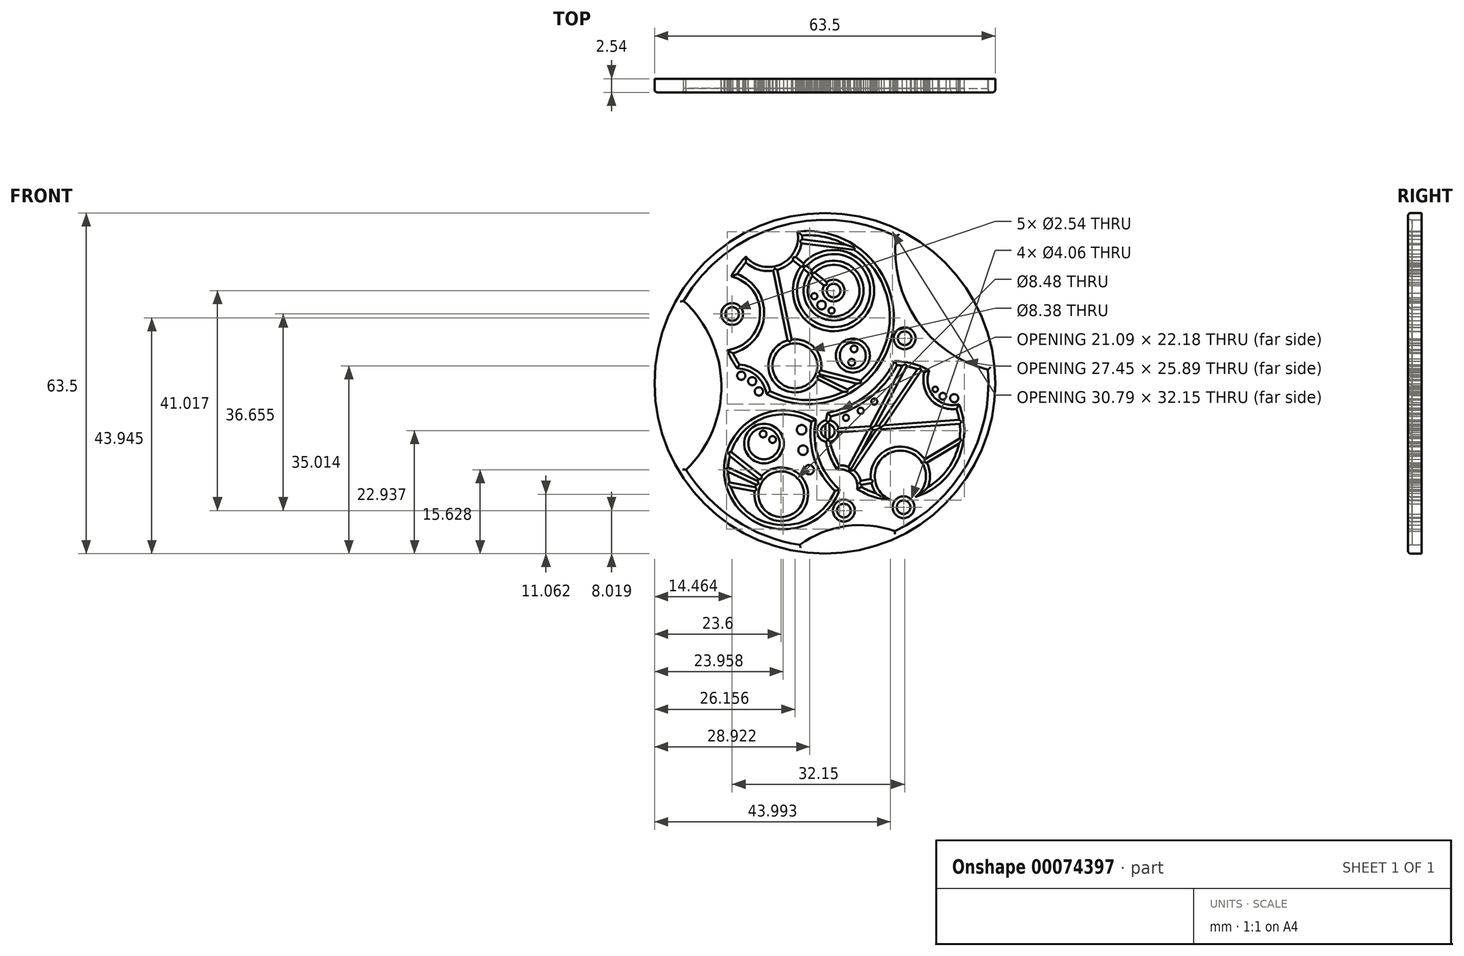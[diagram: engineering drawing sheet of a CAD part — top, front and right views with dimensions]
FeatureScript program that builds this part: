
annotation { "Feature Type Name" : "Feature", "Feature Type Description" : "" }
export const myFeature = defineFeature(function(context is Context, id is Id, definition is map)
    precondition{}
    {
        {
            var Q0;
            Q0=qCreatedBy(makeId("Front.planeOp"),FACE);
            var sketch = newSketch(context, id + "F0", { "sketchPlane" : qUnion([Q0])});
            skCircle(sketch, "E0", {"center": v(0, 0) * mm, "radius": 31.75 * mm});
            skCircle(sketch, "E1", {"center": v(-8.15, -20.69) * mm, "radius": 5 * mm});
            skCircle(sketch, "E2", {"center": v(-11.36, -11.23) * mm, "radius": 3.69 * mm});
            skArc(sketch, "E3", {"start": v(13.02, -27.56) * mm, "mid": v(26.4, -15.22) * mm, "end": v(30.37, 2.55) * mm});
            skArc(sketch, "E4", {"start": v(-18.22, 6.19) * mm, "mid": v(-17.38, 4.42) * mm, "end": v(-16.33, 2.77) * mm});
            skArc(sketch, "E5", {"start": v(16.87, -21.2) * mm, "mid": v(24.74, -14.34) * mm, "end": v(25, -3.9) * mm});
            skPoint(sketch, "E6", {"position": v(31.75, -0.45) * mm});
            skPoint(sketch, "E7", {"position": v(31.42, -4.58) * mm});
            skPoint(sketch, "E8", {"position": v(30.4, -2.2) * mm});
            skCircle(sketch, "E9", {"center": v(3.54, -23.73) * mm, "radius": 1.27 * mm});
            skCircle(sketch, "E10", {"center": v(14.67, -23.1) * mm, "radius": 1.27 * mm});
            skCircle(sketch, "E11", {"center": v(-5.6, 3.26) * mm, "radius": 4.95 * mm});
            skCircle(sketch, "E12", {"center": v(5.2, 5.17) * mm, "radius": 3.18 * mm});
            skCircle(sketch, "E13", {"center": v(1.62, 17.29) * mm, "radius": 1.27 * mm});
            skCircle(sketch, "E14", {"center": v(1.62, 17.29) * mm, "radius": 5.58 * mm});
            skCircle(sketch, "E15", {"center": v(1.62, 17.29) * mm, "radius": 6.81 * mm});
            skCircle(sketch, "E16", {"center": v(14.86, 8.39) * mm, "radius": 1.27 * mm});
            skCircle(sketch, "E17", {"center": v(-17.29, 12.92) * mm, "radius": 1.27 * mm});
            skArc(sketch, "E18", {"start": v(16.87, -21.2) * mm, "mid": v(13.48, -12.59) * mm, "end": v(12.28, -21.76) * mm});
            skArc(sketch, "E19", {"start": v(6.02, -19.73) * mm, "mid": v(5.1, -16.94) * mm, "end": v(2.3, -16.1) * mm});
            skArc(sketch, "E20.trimOffspring", {"start": v(6.02, -19.73) * mm, "mid": v(9.02, -21.15) * mm, "end": v(12.28, -21.76) * mm});
            skArc(sketch, "E21", {"start": v(-1.7, -6.78) * mm, "mid": v(-1.2, -13.9) * mm, "end": v(2.75, -19.84) * mm});
            skPoint(sketch, "E22.center.orphan", {"position": v(-7.7, -16.12) * mm});
            skArc(sketch, "E23", {"start": v(19.46, 2.42) * mm, "mid": v(20.27, -2.46) * mm, "end": v(25, -3.9) * mm});
            skArc(sketch, "E24.trimOffspring", {"start": v(19.46, 2.42) * mm, "mid": v(16.34, 3.7) * mm, "end": v(13, 4.13) * mm});
            skArc(sketch, "E25", {"start": v(0.49, -5.54) * mm, "mid": v(7.84, -2.14) * mm, "end": v(13, 4.13) * mm});
            skArc(sketch, "E26.trimOffspring", {"start": v(0.49, -5.54) * mm, "mid": v(0.25, -11.02) * mm, "end": v(2.3, -16.1) * mm});
            skArc(sketch, "E27", {"start": v(-18.22, 6.19) * mm, "mid": v(-12.08, 12.73) * mm, "end": v(-17.46, 19.92) * mm});
            skArc(sketch, "E28", {"start": v(-14.73, 23.6) * mm, "mid": v(-8.13, 22.24) * mm, "end": v(-5.12, 28.27) * mm});
            skArc(sketch, "E29.trimOffspring", {"start": v(-14.73, 23.6) * mm, "mid": v(-16.23, 21.86) * mm, "end": v(-17.46, 19.92) * mm});
            skArc(sketch, "E30", {"start": v(-10.9, -1.97) * mm, "mid": v(-12.74, 1.39) * mm, "end": v(-16.33, 2.77) * mm});
            skArc(sketch, "E31.trimOffspring", {"start": v(-10.9, -1.97) * mm, "mid": v(12.57, 9.22) * mm, "end": v(-5.12, 28.27) * mm});
            skArc(sketch, "E32", {"start": v(-1.7, -6.78) * mm, "mid": v(-18.2, -19.7) * mm, "end": v(2.75, -19.84) * mm});
            skCircle(sketch, "E33", {"center": v(-11.5, -9.46) * mm, "radius": 0.64 * mm});
            skCircle(sketch, "E34", {"center": v(-9.74, -10.48) * mm, "radius": 0.64 * mm});
            skCircle(sketch, "E35.0", {"center": v(-11.36, -11.23) * mm, "radius": 2.92 * mm});
            skArc(sketch, "E36.0", {"start": v(-2.54, -7.16) * mm, "mid": v(-17.48, -19.45) * mm, "end": v(1.85, -20.05) * mm});
            skArc(sketch, "E36.1", {"start": v(-2.54, -7.16) * mm, "mid": v(-1.92, -14.15) * mm, "end": v(1.85, -20.05) * mm});
            skCircle(sketch, "E37.0", {"center": v(-8.15, -20.69) * mm, "radius": 4.24 * mm});
            skCircle(sketch, "E38", {"center": v(-4.35, -8.66) * mm, "radius": 0.89 * mm});
            skCircle(sketch, "E39", {"center": v(-4.07, -12.46) * mm, "radius": 0.89 * mm});
            skCircle(sketch, "E40", {"center": v(-2.93, -16.1) * mm, "radius": 0.89 * mm});
            skArc(sketch, "E41.0", {"start": v(19.23, -19.31) * mm, "mid": v(24.47, -12.99) * mm, "end": v(24.52, -4.78) * mm});
            skArc(sketch, "E41.1", {"start": v(18.53, 2.05) * mm, "mid": v(19.7, -2.96) * mm, "end": v(24.52, -4.78) * mm});
            skArc(sketch, "E41.2", {"start": v(19.23, -19.31) * mm, "mid": v(13.39, -11.83) * mm, "end": v(9.53, -20.5) * mm});
            skArc(sketch, "E41.3", {"start": v(18.53, 2.05) * mm, "mid": v(16.06, 2.98) * mm, "end": v(13.45, 3.36) * mm});
            skArc(sketch, "E41.4", {"start": v(6.82, -19.33) * mm, "mid": v(8.14, -20) * mm, "end": v(9.53, -20.5) * mm});
            skArc(sketch, "E41.5", {"start": v(6.82, -19.33) * mm, "mid": v(5.64, -16.4) * mm, "end": v(2.68, -15.29) * mm});
            skArc(sketch, "E41.6", {"start": v(1.11, -6.18) * mm, "mid": v(1, -10.89) * mm, "end": v(2.68, -15.29) * mm});
            skArc(sketch, "E41.7", {"start": v(1.11, -6.18) * mm, "mid": v(8.31, -2.74) * mm, "end": v(13.45, 3.36) * mm});
            skArc(sketch, "E42.0", {"start": v(-14.71, 22.5) * mm, "mid": v(-15.56, 21.47) * mm, "end": v(-16.32, 20.37) * mm});
            skArc(sketch, "E42.1", {"start": v(-10.21, -1.47) * mm, "mid": v(11.78, 9.16) * mm, "end": v(-4.27, 27.58) * mm});
            skArc(sketch, "E42.2", {"start": v(-10.21, -1.47) * mm, "mid": v(-12.24, 1.96) * mm, "end": v(-15.92, 3.5) * mm});
            skArc(sketch, "E42.3", {"start": v(-14.71, 22.5) * mm, "mid": v(-7.8, 21.56) * mm, "end": v(-4.27, 27.58) * mm});
            skArc(sketch, "E42.4", {"start": v(-17.14, 5.61) * mm, "mid": v(-16.57, 4.54) * mm, "end": v(-15.92, 3.5) * mm});
            skArc(sketch, "E42.5", {"start": v(-17.14, 5.61) * mm, "mid": v(-11.32, 12.7) * mm, "end": v(-16.32, 20.37) * mm});
            skCircle(sketch, "E43.0", {"center": v(1.62, 17.29) * mm, "radius": 7.57 * mm});
            skCircle(sketch, "E44.0", {"center": v(1.62, 17.29) * mm, "radius": 4.82 * mm});
            skCircle(sketch, "E45", {"center": v(0.55, -8.9) * mm, "radius": 1.27 * mm});
            skCircle(sketch, "E46.0", {"center": v(0.55, -8.9) * mm, "radius": 2.03 * mm});
            skCircle(sketch, "E47.0", {"center": v(3.54, -23.73) * mm, "radius": 2.03 * mm});
            skCircle(sketch, "E48.0", {"center": v(14.67, -23.1) * mm, "radius": 2.03 * mm});
            skCircle(sketch, "E49.0", {"center": v(14.86, 8.39) * mm, "radius": 2.03 * mm});
            skCircle(sketch, "E50.0", {"center": v(5.2, 5.17) * mm, "radius": 2.41 * mm});
            skCircle(sketch, "E51.0", {"center": v(-5.6, 3.26) * mm, "radius": 4.2 * mm});
            skCircle(sketch, "E52.0", {"center": v(1.62, 17.29) * mm, "radius": 2.03 * mm});
            skCircle(sketch, "E53.0", {"center": v(-17.29, 12.92) * mm, "radius": 2.03 * mm});
            skCircle(sketch, "E54", {"center": v(24.1, -2.78) * mm, "radius": 0.76 * mm});
            skCircle(sketch, "E55", {"center": v(21.97, -2.41) * mm, "radius": 0.64 * mm});
            skCircle(sketch, "E56", {"center": v(20.57, -1.12) * mm, "radius": 0.5 * mm});
            skCircle(sketch, "E57", {"center": v(3.93, -6.43) * mm, "radius": 0.57 * mm});
            skCircle(sketch, "E58", {"center": v(6.68, -5.12) * mm, "radius": 0.57 * mm});
            skCircle(sketch, "E59", {"center": v(9.2, -3.41) * mm, "radius": 0.57 * mm});
            skCircle(sketch, "E60", {"center": v(5.44, 6.42) * mm, "radius": 0.64 * mm});
            skCircle(sketch, "E61", {"center": v(5, 3.92) * mm, "radius": 0.64 * mm});
            skCircle(sketch, "E62", {"center": v(-15.6, 1.42) * mm, "radius": 0.76 * mm});
            skCircle(sketch, "E63", {"center": v(-13.54, 0.4) * mm, "radius": 0.76 * mm});
            skCircle(sketch, "E64", {"center": v(-12.3, -1.52) * mm, "radius": 0.76 * mm});
            skCircle(sketch, "E65", {"center": v(-1.97, 16.23) * mm, "radius": 0.57 * mm});
            skCircle(sketch, "E66", {"center": v(-0.62, 14.58) * mm, "radius": 0.8 * mm});
            skCircle(sketch, "E67", {"center": v(1.25, 13.57) * mm, "radius": 0.57 * mm});
            skLineSegment(sketch, "E68", {"start": v(-5.67, 23.24) * mm, "end": v(0.04, 18.57) * mm});
            skLineSegment(sketch, "E69.0", {"start": v(-5.92, 22.95) * mm, "end": v(-0.17, 18.25) * mm});
            skLineSegment(sketch, "E70.0", {"start": v(-5.44, 23.54) * mm, "end": v(0.31, 18.84) * mm});
            skLineSegment(sketch, "E71", {"start": v(-9.27, 21.06) * mm, "end": v(-6.6, 8.11) * mm});
            skLineSegment(sketch, "E72.0", {"start": v(-9.65, 21) * mm, "end": v(-6.97, 8.02) * mm});
            skLineSegment(sketch, "E73.0", {"start": v(-8.9, 21.14) * mm, "end": v(-6.22, 8.18) * mm});
            skLineSegment(sketch, "E74", {"start": v(-4.3, 26.46) * mm, "end": v(4.72, 25.37) * mm});
            skLineSegment(sketch, "E75.0", {"start": v(-4.36, 26.08) * mm, "end": v(5.44, 24.9) * mm});
            skLineSegment(sketch, "E76.0", {"start": v(-4.27, 26.84) * mm, "end": v(3.85, 25.86) * mm});
            skPoint(sketch, "E77.orphan", {"position": v(6.37, 25.17) * mm});
            skLineSegment(sketch, "E78", {"start": v(-0.8, 2.04) * mm, "end": v(6.3, 0.23) * mm});
            skLineSegment(sketch, "E79", {"start": v(-1.15, 1.07) * mm, "end": v(3.82, -1.39) * mm});
            skLineSegment(sketch, "E80.0", {"start": v(-1.34, 0.74) * mm, "end": v(3.4, -1.6) * mm});
            skLineSegment(sketch, "E81.0", {"start": v(-1, 1.42) * mm, "end": v(4.23, -1.16) * mm});
            skLineSegment(sketch, "E82.0", {"start": v(-0.9, 1.68) * mm, "end": v(5.93, -0.06) * mm});
            skLineSegment(sketch, "E83.0", {"start": v(-0.71, 2.41) * mm, "end": v(6.67, 0.53) * mm});
            skPoint(sketch, "E84.orphan", {"position": v(7.22, 0) * mm});
            skLineSegment(sketch, "E85", {"start": v(6.77, -18.56) * mm, "end": v(8.6, -18.25) * mm});
            skLineSegment(sketch, "E86", {"start": v(18.82, -14.49) * mm, "end": v(25.05, -10.75) * mm});
            skLineSegment(sketch, "E87.0", {"start": v(6.82, -18.94) * mm, "end": v(8.68, -18.63) * mm});
            skLineSegment(sketch, "E88.0", {"start": v(6.69, -18.19) * mm, "end": v(8.56, -17.87) * mm});
            skLineSegment(sketch, "E89.0", {"start": v(19, -14.82) * mm, "end": v(24.96, -11.25) * mm});
            skLineSegment(sketch, "E90.0", {"start": v(18.6, -14.17) * mm, "end": v(25.12, -10.27) * mm});
            skLineSegment(sketch, "E91.trimOffspring", {"start": v(2.58, -8.77) * mm, "end": v(25.1, -7.19) * mm});
            skLineSegment(sketch, "E92.0", {"start": v(2.57, -9.15) * mm, "end": v(25.14, -7.57) * mm});
            skLineSegment(sketch, "E93.0", {"start": v(2.52, -8.39) * mm, "end": v(25.04, -6.8) * mm});
            skLineSegment(sketch, "E94.trimOffspring", {"start": v(25.8, -6.76) * mm, "end": v(25.83, -6.75) * mm});
            skLineSegment(sketch, "E95", {"start": v(4.74, -15.74) * mm, "end": v(14.85, 3.23) * mm});
            skLineSegment(sketch, "E96", {"start": v(5.1, -15.96) * mm, "end": v(17.6, 2.48) * mm});
            skLineSegment(sketch, "E97.0", {"start": v(6.6, -13.07) * mm, "end": v(15.24, 3.16) * mm});
            skLineSegment(sketch, "E98.0", {"start": v(4.4, -15.58) * mm, "end": v(14.45, 3.28) * mm});
            skLineSegment(sketch, "E99.0", {"start": v(5.4, -16.19) * mm, "end": v(17.95, 2.32) * mm});
            skLineSegment(sketch, "E100.trimOffspring", {"start": v(6.6, -13.07) * mm, "end": v(17.23, 2.62) * mm});
            skPoint(sketch, "E101", {"position": v(14.82, 4) * mm});
            skLineSegment(sketch, "E102", {"start": v(-13.06, -19.75) * mm, "end": v(-17.66, -18.87) * mm});
            skLineSegment(sketch, "E103", {"start": v(-12.69, -18.58) * mm, "end": v(-18.03, -16.1) * mm});
            skLineSegment(sketch, "E104", {"start": v(-12.07, -17.58) * mm, "end": v(-17.6, -13.18) * mm});
            skLineSegment(sketch, "E105.0", {"start": v(-11.82, -17.29) * mm, "end": v(-17.48, -12.79) * mm});
            skLineSegment(sketch, "E106.0", {"start": v(-12.3, -17.88) * mm, "end": v(-17.72, -13.57) * mm});
            skLineSegment(sketch, "E107.0", {"start": v(-12.83, -18.93) * mm, "end": v(-18.03, -16.52) * mm});
            skLineSegment(sketch, "E108.0", {"start": v(-12.51, -18.24) * mm, "end": v(-18.02, -15.68) * mm});
            skLineSegment(sketch, "E109.0", {"start": v(-12.98, -19.37) * mm, "end": v(-17.76, -18.46) * mm});
            skLineSegment(sketch, "E110.0", {"start": v(-13.12, -20.12) * mm, "end": v(-17.54, -19.28) * mm});
            skArc(sketch, "E111", {"start": v(-25.87, -16.12) * mm, "mid": v(-19.3, -0.29) * mm, "end": v(-26.34, 15.34) * mm});
            skArc(sketch, "E112", {"start": v(13.28, 27.44) * mm, "mid": v(17.13, 11.77) * mm, "end": v(30.37, 2.55) * mm});
            skArc(sketch, "E113", {"start": v(13.02, -27.56) * mm, "mid": v(3.86, -26.64) * mm, "end": v(-4.67, -30.12) * mm});
            skArc(sketch, "E114.trimOffspring", {"start": v(-25.87, -16.12) * mm, "mid": v(-16.8, -25.44) * mm, "end": v(-4.67, -30.12) * mm});
            skArc(sketch, "E115.trimOffspring", {"start": v(13.28, 27.44) * mm, "mid": v(-8.9, 29.15) * mm, "end": v(-26.34, 15.34) * mm});
            skSolve(sketch);
        }
        {
            var Q0;
            Q0=makeQuery(id+"F0.imprint","IMPRINT",FACE,{"disambiguationData":[TD([[makeQuery(id+"F0.imprint","IMPRINT",EDGE,{"derivedFrom":sQuery(id+"F0.wireOp",EDGE,"E0")}),1.0]])]});
            var Q1;
            Q1=makeQuery(id+"F0.imprint","IMPRINT",FACE,{"disambiguationData":[TD([[makeQuery(id+"F0.imprint","IMPRINT",EDGE,{"derivedFrom":sQuery(id+"F0.wireOp",EDGE,"E17")}),-1.0]])]});
            var Q2;
            Q2=makeQuery(id+"F0.imprint","IMPRINT",FACE,{"disambiguationData":[TD([[makeQuery(id+"F0.imprint","IMPRINT",EDGE,{"derivedFrom":sQuery(id+"F0.wireOp",EDGE,"E4")}),1.0]])]});
            var Q3;
            {var subQ0=sQuery(id+"F0.wireOp",EDGE,"E71");Q3=makeQuery(id+"F0.imprint","IMPRINT",FACE,{"disambiguationData":[TD([[makeQuery(id+"F0.imprint","IMPRINT",EDGE,{"derivedFrom":subQ0}),-1.0]])]});}
            var Q4;
            {var subQ0=sQuery(id+"F0.wireOp",EDGE,"E71");Q4=makeQuery(id+"F0.imprint","IMPRINT",FACE,{"disambiguationData":[TD([[makeQuery(id+"F0.imprint","IMPRINT",EDGE,{"derivedFrom":subQ0}),1.0]])]});}
            var Q5;
            {var subQ0=sQuery(id+"F0.wireOp",EDGE,"E68");var subQ1=sQuery(id+"F0.wireOp",EDGE,"E42.3");var subQ2=makeQuery(id+"F0.imprint","INTERSECT",VERTEX,{"derivedFrom":[subQ1,subQ0]});Q5=makeQuery(id+"F0.imprint","IMPRINT",FACE,{"disambiguationData":[TD([[makeQuery(id+"F0.imprint","IMPRINT",EDGE,{"disambiguationData":[TD([[subQ2,1.0]])],"derivedFrom":subQ1}),-1.0]])]});}
            var Q6;
            {var subQ0=sQuery(id+"F0.wireOp",EDGE,"E68");var subQ1=sQuery(id+"F0.wireOp",EDGE,"E42.3");var subQ2=makeQuery(id+"F0.imprint","INTERSECT",VERTEX,{"derivedFrom":[subQ1,subQ0]});Q6=makeQuery(id+"F0.imprint","IMPRINT",FACE,{"disambiguationData":[TD([[makeQuery(id+"F0.imprint","IMPRINT",EDGE,{"disambiguationData":[TD([[subQ2,-1.0]])],"derivedFrom":subQ1}),-1.0]])]});}
            var Q7;
            {var subQ0=sQuery(id+"F0.wireOp",EDGE,"E68");var subQ1=sQuery(id+"F0.wireOp",EDGE,"E15");var subQ2=makeQuery(id+"F0.imprint","INTERSECT",VERTEX,{"derivedFrom":[subQ1,subQ0]});Q7=makeQuery(id+"F0.imprint","IMPRINT",FACE,{"disambiguationData":[TD([[makeQuery(id+"F0.imprint","IMPRINT",EDGE,{"disambiguationData":[TD([[subQ2,-1.0]])],"derivedFrom":subQ1}),-1.0]])]});}
            var Q8;
            {var subQ0=sQuery(id+"F0.wireOp",EDGE,"E68");var subQ1=sQuery(id+"F0.wireOp",EDGE,"E15");var subQ2=makeQuery(id+"F0.imprint","INTERSECT",VERTEX,{"derivedFrom":[subQ1,subQ0]});Q8=makeQuery(id+"F0.imprint","IMPRINT",FACE,{"disambiguationData":[TD([[makeQuery(id+"F0.imprint","IMPRINT",EDGE,{"disambiguationData":[TD([[subQ2,1.0]])],"derivedFrom":subQ1}),-1.0]])]});}
            var Q9;
            {var subQ0=sQuery(id+"F0.wireOp",EDGE,"E68");var subQ1=sQuery(id+"F0.wireOp",EDGE,"E14");var subQ2=makeQuery(id+"F0.imprint","INTERSECT",VERTEX,{"derivedFrom":[subQ1,subQ0]});Q9=makeQuery(id+"F0.imprint","IMPRINT",FACE,{"disambiguationData":[TD([[makeQuery(id+"F0.imprint","IMPRINT",EDGE,{"disambiguationData":[TD([[subQ2,-1.0]])],"derivedFrom":subQ1}),-1.0]])]});}
            var Q10;
            {var subQ0=sQuery(id+"F0.wireOp",EDGE,"E68");var subQ1=sQuery(id+"F0.wireOp",EDGE,"E14");var subQ2=makeQuery(id+"F0.imprint","INTERSECT",VERTEX,{"derivedFrom":[subQ1,subQ0]});Q10=makeQuery(id+"F0.imprint","IMPRINT",FACE,{"disambiguationData":[TD([[makeQuery(id+"F0.imprint","IMPRINT",EDGE,{"disambiguationData":[TD([[subQ2,1.0]])],"derivedFrom":subQ1}),-1.0]])]});}
            var Q11;
            {var subQ0=sQuery(id+"F0.wireOp",EDGE,"E68");var subQ1=sQuery(id+"F0.wireOp",EDGE,"E14");var subQ2=makeQuery(id+"F0.imprint","INTERSECT",VERTEX,{"derivedFrom":[subQ1,subQ0]});Q11=makeQuery(id+"F0.imprint","IMPRINT",FACE,{"disambiguationData":[TD([[makeQuery(id+"F0.imprint","IMPRINT",EDGE,{"disambiguationData":[TD([[subQ2,-1.0]])],"derivedFrom":subQ1}),1.0]])]});}
            var Q12;
            {var subQ0=sQuery(id+"F0.wireOp",EDGE,"E68");var subQ1=sQuery(id+"F0.wireOp",EDGE,"E14");var subQ2=makeQuery(id+"F0.imprint","INTERSECT",VERTEX,{"derivedFrom":[subQ1,subQ0]});Q12=makeQuery(id+"F0.imprint","IMPRINT",FACE,{"disambiguationData":[TD([[makeQuery(id+"F0.imprint","IMPRINT",EDGE,{"disambiguationData":[TD([[subQ2,1.0]])],"derivedFrom":subQ1}),1.0]])]});}
            var Q13;
            {var subQ0=sQuery(id+"F0.wireOp",EDGE,"E68");var subQ1=sQuery(id+"F0.wireOp",EDGE,"E44.0");var subQ2=makeQuery(id+"F0.imprint","INTERSECT",VERTEX,{"derivedFrom":[subQ1,subQ0]});Q13=makeQuery(id+"F0.imprint","IMPRINT",FACE,{"disambiguationData":[TD([[makeQuery(id+"F0.imprint","IMPRINT",EDGE,{"disambiguationData":[TD([[subQ2,-1.0]])],"derivedFrom":subQ1}),1.0]])]});}
            var Q14;
            {var subQ0=sQuery(id+"F0.wireOp",EDGE,"E68");var subQ1=sQuery(id+"F0.wireOp",EDGE,"E44.0");var subQ2=makeQuery(id+"F0.imprint","INTERSECT",VERTEX,{"derivedFrom":[subQ1,subQ0]});Q14=makeQuery(id+"F0.imprint","IMPRINT",FACE,{"disambiguationData":[TD([[makeQuery(id+"F0.imprint","IMPRINT",EDGE,{"disambiguationData":[TD([[subQ2,1.0]])],"derivedFrom":subQ1}),1.0]])]});}
            var Q15;
            Q15=makeQuery(id+"F0.imprint","IMPRINT",FACE,{"disambiguationData":[TD([[makeQuery(id+"F0.imprint","IMPRINT",EDGE,{"derivedFrom":sQuery(id+"F0.wireOp",EDGE,"E13")}),-1.0]])]});
            var Q16;
            Q16=makeQuery(id+"F0.imprint","IMPRINT",FACE,{"disambiguationData":[TD([[makeQuery(id+"F0.imprint","IMPRINT",EDGE,{"derivedFrom":sQuery(id+"F0.wireOp",EDGE,"E65")}),1.0]])]});
            var Q17;
            Q17=makeQuery(id+"F0.imprint","IMPRINT",FACE,{"disambiguationData":[TD([[makeQuery(id+"F0.imprint","IMPRINT",EDGE,{"derivedFrom":sQuery(id+"F0.wireOp",EDGE,"E66")}),1.0]])]});
            var Q18;
            Q18=makeQuery(id+"F0.imprint","IMPRINT",FACE,{"disambiguationData":[TD([[makeQuery(id+"F0.imprint","IMPRINT",EDGE,{"derivedFrom":sQuery(id+"F0.wireOp",EDGE,"E67")}),1.0]])]});
            var Q19;
            {var subQ0=sQuery(id+"F0.wireOp",EDGE,"E70.0");var subQ1=sQuery(id+"F0.wireOp",EDGE,"E14");var subQ2=makeQuery(id+"F0.imprint","INTERSECT",VERTEX,{"derivedFrom":[subQ1,subQ0]});Q19=makeQuery(id+"F0.imprint","IMPRINT",FACE,{"disambiguationData":[TD([[makeQuery(id+"F0.imprint","IMPRINT",EDGE,{"disambiguationData":[TD([[subQ2,1.0]])],"derivedFrom":subQ1}),1.0]])]});}
            var Q20;
            {var subQ0=sQuery(id+"F0.wireOp",EDGE,"E70.0");var subQ1=sQuery(id+"F0.wireOp",EDGE,"E15");var subQ2=makeQuery(id+"F0.imprint","INTERSECT",VERTEX,{"derivedFrom":[subQ1,subQ0]});Q20=makeQuery(id+"F0.imprint","IMPRINT",FACE,{"disambiguationData":[TD([[makeQuery(id+"F0.imprint","IMPRINT",EDGE,{"disambiguationData":[TD([[subQ2,1.0]])],"derivedFrom":subQ1}),-1.0]])]});}
            var Q21;
            {var subQ0=sQuery(id+"F0.wireOp",EDGE,"E74");Q21=makeQuery(id+"F0.imprint","IMPRINT",FACE,{"disambiguationData":[TD([[makeQuery(id+"F0.imprint","IMPRINT",EDGE,{"derivedFrom":subQ0}),1.0]])]});}
            var Q22;
            {var subQ0=sQuery(id+"F0.wireOp",EDGE,"E74");Q22=makeQuery(id+"F0.imprint","IMPRINT",FACE,{"disambiguationData":[TD([[makeQuery(id+"F0.imprint","IMPRINT",EDGE,{"derivedFrom":subQ0}),-1.0]])]});}
            var Q23;
            Q23=makeQuery(id+"F0.imprint","IMPRINT",FACE,{"disambiguationData":[TD([[makeQuery(id+"F0.imprint","IMPRINT",EDGE,{"derivedFrom":sQuery(id+"F0.wireOp",EDGE,"E12")}),1.0]])]});
            var Q24;
            Q24=makeQuery(id+"F0.imprint","IMPRINT",FACE,{"disambiguationData":[TD([[makeQuery(id+"F0.imprint","IMPRINT",EDGE,{"derivedFrom":sQuery(id+"F0.wireOp",EDGE,"E51.0")}),-1.0]])]});
            var Q25;
            Q25=makeQuery(id+"F0.imprint","IMPRINT",FACE,{"disambiguationData":[TD([[makeQuery(id+"F0.imprint","IMPRINT",EDGE,{"derivedFrom":sQuery(id+"F0.wireOp",EDGE,"E16")}),-1.0]])]});
            var Q26;
            {var subQ0=sQuery(id+"F0.wireOp",EDGE,"E79");Q26=makeQuery(id+"F0.imprint","IMPRINT",FACE,{"disambiguationData":[TD([[makeQuery(id+"F0.imprint","IMPRINT",EDGE,{"derivedFrom":subQ0}),-1.0]])]});}
            var Q27;
            {var subQ0=sQuery(id+"F0.wireOp",EDGE,"E79");Q27=makeQuery(id+"F0.imprint","IMPRINT",FACE,{"disambiguationData":[TD([[makeQuery(id+"F0.imprint","IMPRINT",EDGE,{"derivedFrom":subQ0}),1.0]])]});}
            var Q28;
            {var subQ0=sQuery(id+"F0.wireOp",EDGE,"E78");Q28=makeQuery(id+"F0.imprint","IMPRINT",FACE,{"disambiguationData":[TD([[makeQuery(id+"F0.imprint","IMPRINT",EDGE,{"derivedFrom":subQ0}),-1.0]])]});}
            var Q29;
            {var subQ0=sQuery(id+"F0.wireOp",EDGE,"E78");Q29=makeQuery(id+"F0.imprint","IMPRINT",FACE,{"disambiguationData":[TD([[makeQuery(id+"F0.imprint","IMPRINT",EDGE,{"derivedFrom":subQ0}),1.0]])]});}
            var Q30;
            Q30=makeQuery(id+"F0.imprint","IMPRINT",FACE,{"disambiguationData":[TD([[makeQuery(id+"F0.imprint","IMPRINT",EDGE,{"derivedFrom":sQuery(id+"F0.wireOp",EDGE,"E62")}),1.0]])]});
            var Q31;
            Q31=makeQuery(id+"F0.imprint","IMPRINT",FACE,{"disambiguationData":[TD([[makeQuery(id+"F0.imprint","IMPRINT",EDGE,{"derivedFrom":sQuery(id+"F0.wireOp",EDGE,"E63")}),1.0]])]});
            var Q32;
            Q32=makeQuery(id+"F0.imprint","IMPRINT",FACE,{"disambiguationData":[TD([[makeQuery(id+"F0.imprint","IMPRINT",EDGE,{"derivedFrom":sQuery(id+"F0.wireOp",EDGE,"E64")}),1.0]])]});
            var Q33;
            {var subQ3=sQuery(id+"F0.wireOp",EDGE,"E32");Q33=makeQuery(id+"F0.imprint","IMPRINT",FACE,{"disambiguationData":[TD([[makeQuery(id+"F0.imprint","IMPRINT",EDGE,{"derivedFrom":subQ3}),1.0]])]});}
            var Q34;
            {var subQ0=sQuery(id+"F0.wireOp",EDGE,"E46.0");var subQ1=sQuery(id+"F0.wireOp",EDGE,"E26.trimOffspring");var subQ2=makeQuery(id+"F0.imprint","INTERSECT",VERTEX,{"disambiguationData":[OD(0.0)],"derivedFrom":[subQ1,subQ0]});Q34=makeQuery(id+"F0.imprint","IMPRINT",FACE,{"disambiguationData":[TD([[makeQuery(id+"F0.imprint","IMPRINT",EDGE,{"disambiguationData":[TD([[subQ2,-1.0]])],"derivedFrom":subQ1}),-1.0]])]});}
            var Q35;
            {var subQ0=sQuery(id+"F0.wireOp",EDGE,"E46.0");var subQ4=sQuery(id+"F0.wireOp",EDGE,"E41.6");var subQ7=makeQuery(id+"F0.imprint","INTERSECT",VERTEX,{"disambiguationData":[OD(0.0)],"derivedFrom":[subQ4,subQ0]});Q35=makeQuery(id+"F0.imprint","IMPRINT",FACE,{"disambiguationData":[TD([[makeQuery(id+"F0.imprint","IMPRINT",EDGE,{"disambiguationData":[TD([[subQ7,-1.0]])],"derivedFrom":subQ4}),1.0]])]});}
            var Q36;
            {var subQ0=sQuery(id+"F0.wireOp",EDGE,"E46.0");var subQ1=sQuery(id+"F0.wireOp",EDGE,"E26.trimOffspring");var subQ2=makeQuery(id+"F0.imprint","INTERSECT",VERTEX,{"disambiguationData":[OD(0.0)],"derivedFrom":[subQ1,subQ0]});Q36=makeQuery(id+"F0.imprint","IMPRINT",FACE,{"disambiguationData":[TD([[makeQuery(id+"F0.imprint","IMPRINT",EDGE,{"disambiguationData":[TD([[subQ2,-1.0]])],"derivedFrom":subQ1}),1.0]])]});}
            var Q37;
            {var subQ0=sQuery(id+"F0.wireOp",EDGE,"E45");var subQ1=sQuery(id+"F0.wireOp",EDGE,"E26.trimOffspring");var subQ2=makeQuery(id+"F0.imprint","INTERSECT",VERTEX,{"disambiguationData":[OD(0.0)],"derivedFrom":[subQ1,subQ0]});Q37=makeQuery(id+"F0.imprint","IMPRINT",FACE,{"disambiguationData":[TD([[makeQuery(id+"F0.imprint","IMPRINT",EDGE,{"disambiguationData":[TD([[subQ2,-1.0]])],"derivedFrom":subQ1}),1.0]])]});}
            var Q38;
            {var subQ0=sQuery(id+"F0.wireOp",EDGE,"E45");var subQ1=sQuery(id+"F0.wireOp",EDGE,"E26.trimOffspring");var subQ2=makeQuery(id+"F0.imprint","INTERSECT",VERTEX,{"disambiguationData":[OD(1.0)],"derivedFrom":[subQ1,subQ0]});Q38=makeQuery(id+"F0.imprint","IMPRINT",FACE,{"disambiguationData":[TD([[makeQuery(id+"F0.imprint","IMPRINT",EDGE,{"disambiguationData":[TD([[subQ2,-1.0]])],"derivedFrom":subQ1}),1.0]])]});}
            var Q39;
            Q39=makeQuery(id+"F0.imprint","IMPRINT",FACE,{"disambiguationData":[TD([[makeQuery(id+"F0.imprint","IMPRINT",EDGE,{"derivedFrom":sQuery(id+"F0.wireOp",EDGE,"E2")}),1.0]])]});
            var Q40;
            Q40=makeQuery(id+"F0.imprint","IMPRINT",FACE,{"disambiguationData":[TD([[makeQuery(id+"F0.imprint","IMPRINT",EDGE,{"derivedFrom":sQuery(id+"F0.wireOp",EDGE,"E37.0")}),-1.0]])]});
            var Q41;
            Q41=makeQuery(id+"F0.imprint","IMPRINT",FACE,{"disambiguationData":[TD([[makeQuery(id+"F0.imprint","IMPRINT",EDGE,{"derivedFrom":sQuery(id+"F0.wireOp",EDGE,"E38")}),1.0]])]});
            var Q42;
            Q42=makeQuery(id+"F0.imprint","IMPRINT",FACE,{"disambiguationData":[TD([[makeQuery(id+"F0.imprint","IMPRINT",EDGE,{"derivedFrom":sQuery(id+"F0.wireOp",EDGE,"E39")}),1.0]])]});
            var Q43;
            Q43=makeQuery(id+"F0.imprint","IMPRINT",FACE,{"disambiguationData":[TD([[makeQuery(id+"F0.imprint","IMPRINT",EDGE,{"derivedFrom":sQuery(id+"F0.wireOp",EDGE,"E40")}),1.0]])]});
            var Q44;
            Q44=makeQuery(id+"F0.imprint","IMPRINT",FACE,{"disambiguationData":[TD([[makeQuery(id+"F0.imprint","IMPRINT",EDGE,{"derivedFrom":sQuery(id+"F0.wireOp",EDGE,"E9")}),-1.0]])]});
            var Q45;
            Q45=makeQuery(id+"F0.imprint","IMPRINT",FACE,{"disambiguationData":[TD([[makeQuery(id+"F0.imprint","IMPRINT",EDGE,{"derivedFrom":sQuery(id+"F0.wireOp",EDGE,"E10")}),-1.0]])]});
            var Q46;
            {var subQ30=sQuery(id+"F0.wireOp",EDGE,"E18");Q46=makeQuery(id+"F0.imprint","IMPRINT",FACE,{"disambiguationData":[TD([[makeQuery(id+"F0.imprint","IMPRINT",EDGE,{"derivedFrom":subQ30}),-1.0]])]});}
            var Q47;
            Q47=makeQuery(id+"F0.imprint","IMPRINT",FACE,{"disambiguationData":[TD([[makeQuery(id+"F0.imprint","IMPRINT",EDGE,{"derivedFrom":sQuery(id+"F0.wireOp",EDGE,"E56")}),1.0]])]});
            var Q48;
            Q48=makeQuery(id+"F0.imprint","IMPRINT",FACE,{"disambiguationData":[TD([[makeQuery(id+"F0.imprint","IMPRINT",EDGE,{"derivedFrom":sQuery(id+"F0.wireOp",EDGE,"E55")}),1.0]])]});
            var Q49;
            Q49=makeQuery(id+"F0.imprint","IMPRINT",FACE,{"disambiguationData":[TD([[makeQuery(id+"F0.imprint","IMPRINT",EDGE,{"derivedFrom":sQuery(id+"F0.wireOp",EDGE,"E54")}),1.0]])]});
            var Q50;
            Q50=makeQuery(id+"F0.imprint","IMPRINT",FACE,{"disambiguationData":[TD([[makeQuery(id+"F0.imprint","IMPRINT",EDGE,{"derivedFrom":sQuery(id+"F0.wireOp",EDGE,"E59")}),1.0]])]});
            var Q51;
            Q51=makeQuery(id+"F0.imprint","IMPRINT",FACE,{"disambiguationData":[TD([[makeQuery(id+"F0.imprint","IMPRINT",EDGE,{"derivedFrom":sQuery(id+"F0.wireOp",EDGE,"E58")}),1.0]])]});
            var Q52;
            Q52=makeQuery(id+"F0.imprint","IMPRINT",FACE,{"disambiguationData":[TD([[makeQuery(id+"F0.imprint","IMPRINT",EDGE,{"derivedFrom":sQuery(id+"F0.wireOp",EDGE,"E57")}),1.0]])]});
            var Q53;
            {var subQ0=sQuery(id+"F0.wireOp",EDGE,"E85");Q53=makeQuery(id+"F0.imprint","IMPRINT",FACE,{"disambiguationData":[TD([[makeQuery(id+"F0.imprint","IMPRINT",EDGE,{"derivedFrom":subQ0}),-1.0]])]});}
            var Q54;
            {var subQ0=sQuery(id+"F0.wireOp",EDGE,"E85");Q54=makeQuery(id+"F0.imprint","IMPRINT",FACE,{"disambiguationData":[TD([[makeQuery(id+"F0.imprint","IMPRINT",EDGE,{"derivedFrom":subQ0}),1.0]])]});}
            var Q55;
            {var subQ0=sQuery(id+"F0.wireOp",EDGE,"E86");Q55=makeQuery(id+"F0.imprint","IMPRINT",FACE,{"disambiguationData":[TD([[makeQuery(id+"F0.imprint","IMPRINT",EDGE,{"derivedFrom":subQ0}),-1.0]])]});}
            var Q56;
            {var subQ0=sQuery(id+"F0.wireOp",EDGE,"E86");Q56=makeQuery(id+"F0.imprint","IMPRINT",FACE,{"disambiguationData":[TD([[makeQuery(id+"F0.imprint","IMPRINT",EDGE,{"derivedFrom":subQ0}),1.0]])]});}
            var Q57;
            {var subQ0=sQuery(id+"F0.wireOp",EDGE,"E91.trimOffspring");var subQ1=sQuery(id+"F0.wireOp",EDGE,"E41.0");var subQ2=makeQuery(id+"F0.imprint","INTERSECT",VERTEX,{"derivedFrom":[subQ1,subQ0]});Q57=makeQuery(id+"F0.imprint","IMPRINT",FACE,{"disambiguationData":[TD([[makeQuery(id+"F0.imprint","IMPRINT",EDGE,{"disambiguationData":[TD([[subQ2,1.0]])],"derivedFrom":subQ1}),1.0]])]});}
            var Q58;
            {var subQ0=sQuery(id+"F0.wireOp",EDGE,"E91.trimOffspring");var subQ1=sQuery(id+"F0.wireOp",EDGE,"E41.0");var subQ2=makeQuery(id+"F0.imprint","INTERSECT",VERTEX,{"derivedFrom":[subQ1,subQ0]});Q58=makeQuery(id+"F0.imprint","IMPRINT",FACE,{"disambiguationData":[TD([[makeQuery(id+"F0.imprint","IMPRINT",EDGE,{"disambiguationData":[TD([[subQ2,-1.0]])],"derivedFrom":subQ1}),1.0]])]});}
            var Q59;
            {var subQ0=sQuery(id+"F0.wireOp",EDGE,"E96");var subQ1=sQuery(id+"F0.wireOp",EDGE,"E41.3");var subQ2=makeQuery(id+"F0.imprint","INTERSECT",VERTEX,{"derivedFrom":[subQ1,subQ0]});Q59=makeQuery(id+"F0.imprint","IMPRINT",FACE,{"disambiguationData":[TD([[makeQuery(id+"F0.imprint","IMPRINT",EDGE,{"disambiguationData":[TD([[subQ2,1.0]])],"derivedFrom":subQ1}),1.0]])]});}
            var Q60;
            {var subQ0=sQuery(id+"F0.wireOp",EDGE,"E96");var subQ1=sQuery(id+"F0.wireOp",EDGE,"E41.3");var subQ2=makeQuery(id+"F0.imprint","INTERSECT",VERTEX,{"derivedFrom":[subQ1,subQ0]});Q60=makeQuery(id+"F0.imprint","IMPRINT",FACE,{"disambiguationData":[TD([[makeQuery(id+"F0.imprint","IMPRINT",EDGE,{"disambiguationData":[TD([[subQ2,-1.0]])],"derivedFrom":subQ1}),1.0]])]});}
            var Q61;
            {var subQ0=sQuery(id+"F0.wireOp",EDGE,"E95");var subQ1=sQuery(id+"F0.wireOp",EDGE,"E41.3");var subQ2=makeQuery(id+"F0.imprint","INTERSECT",VERTEX,{"derivedFrom":[subQ1,subQ0]});Q61=makeQuery(id+"F0.imprint","IMPRINT",FACE,{"disambiguationData":[TD([[makeQuery(id+"F0.imprint","IMPRINT",EDGE,{"disambiguationData":[TD([[subQ2,1.0]])],"derivedFrom":subQ1}),1.0]])]});}
            var Q62;
            {var subQ0=sQuery(id+"F0.wireOp",EDGE,"E95");var subQ1=sQuery(id+"F0.wireOp",EDGE,"E41.3");var subQ2=makeQuery(id+"F0.imprint","INTERSECT",VERTEX,{"derivedFrom":[subQ1,subQ0]});Q62=makeQuery(id+"F0.imprint","IMPRINT",FACE,{"disambiguationData":[TD([[makeQuery(id+"F0.imprint","IMPRINT",EDGE,{"disambiguationData":[TD([[subQ2,-1.0]])],"derivedFrom":subQ1}),1.0]])]});}
            var Q63;
            {var subQ0=sQuery(id+"F0.wireOp",EDGE,"E91.trimOffspring");var subQ1=sQuery(id+"F0.wireOp",EDGE,"E46.0");var subQ2=makeQuery(id+"F0.imprint","INTERSECT",VERTEX,{"derivedFrom":[subQ1,subQ0]});Q63=makeQuery(id+"F0.imprint","IMPRINT",FACE,{"disambiguationData":[TD([[makeQuery(id+"F0.imprint","IMPRINT",EDGE,{"disambiguationData":[TD([[subQ2,-1.0]])],"derivedFrom":subQ1}),-1.0]])]});}
            var Q64;
            {var subQ0=sQuery(id+"F0.wireOp",EDGE,"E91.trimOffspring");var subQ1=sQuery(id+"F0.wireOp",EDGE,"E46.0");var subQ2=makeQuery(id+"F0.imprint","INTERSECT",VERTEX,{"derivedFrom":[subQ1,subQ0]});Q64=makeQuery(id+"F0.imprint","IMPRINT",FACE,{"disambiguationData":[TD([[makeQuery(id+"F0.imprint","IMPRINT",EDGE,{"disambiguationData":[TD([[subQ2,1.0]])],"derivedFrom":subQ1}),-1.0]])]});}
            var Q65;
            {var subQ0=sQuery(id+"F0.wireOp",EDGE,"E95");var subQ1=sQuery(id+"F0.wireOp",EDGE,"E41.5");var subQ2=makeQuery(id+"F0.imprint","INTERSECT",VERTEX,{"derivedFrom":[subQ1,subQ0]});Q65=makeQuery(id+"F0.imprint","IMPRINT",FACE,{"disambiguationData":[TD([[makeQuery(id+"F0.imprint","IMPRINT",EDGE,{"disambiguationData":[TD([[subQ2,-1.0]])],"derivedFrom":subQ1}),-1.0]])]});}
            var Q66;
            {var subQ0=sQuery(id+"F0.wireOp",EDGE,"E95");var subQ1=sQuery(id+"F0.wireOp",EDGE,"E41.5");var subQ2=makeQuery(id+"F0.imprint","INTERSECT",VERTEX,{"derivedFrom":[subQ1,subQ0]});Q66=makeQuery(id+"F0.imprint","IMPRINT",FACE,{"disambiguationData":[TD([[makeQuery(id+"F0.imprint","IMPRINT",EDGE,{"disambiguationData":[TD([[subQ2,1.0]])],"derivedFrom":subQ1}),-1.0]])]});}
            var Q67;
            {var subQ0=sQuery(id+"F0.wireOp",EDGE,"E96");var subQ1=sQuery(id+"F0.wireOp",EDGE,"E41.5");var subQ2=makeQuery(id+"F0.imprint","INTERSECT",VERTEX,{"derivedFrom":[subQ1,subQ0]});Q67=makeQuery(id+"F0.imprint","IMPRINT",FACE,{"disambiguationData":[TD([[makeQuery(id+"F0.imprint","IMPRINT",EDGE,{"disambiguationData":[TD([[subQ2,1.0]])],"derivedFrom":subQ1}),-1.0]])]});}
            var Q68;
            {var subQ0=sQuery(id+"F0.wireOp",EDGE,"E98.0");var subQ1=sQuery(id+"F0.wireOp",EDGE,"E91.trimOffspring");var subQ2=makeQuery(id+"F0.imprint","INTERSECT",VERTEX,{"derivedFrom":[subQ1,subQ0]});Q68=makeQuery(id+"F0.imprint","IMPRINT",FACE,{"disambiguationData":[TD([[makeQuery(id+"F0.imprint","IMPRINT",EDGE,{"disambiguationData":[TD([[subQ2,-1.0]])],"derivedFrom":subQ1}),-1.0]])]});}
            var Q69;
            {var subQ0=sQuery(id+"F0.wireOp",EDGE,"E98.0");var subQ1=sQuery(id+"F0.wireOp",EDGE,"E91.trimOffspring");var subQ2=makeQuery(id+"F0.imprint","INTERSECT",VERTEX,{"derivedFrom":[subQ1,subQ0]});Q69=makeQuery(id+"F0.imprint","IMPRINT",FACE,{"disambiguationData":[TD([[makeQuery(id+"F0.imprint","IMPRINT",EDGE,{"disambiguationData":[TD([[subQ2,-1.0]])],"derivedFrom":subQ1}),1.0]])]});}
            var Q70;
            {var subQ0=sQuery(id+"F0.wireOp",EDGE,"E97.0");var subQ1=sQuery(id+"F0.wireOp",EDGE,"E91.trimOffspring");var subQ2=makeQuery(id+"F0.imprint","INTERSECT",VERTEX,{"derivedFrom":[subQ1,subQ0]});Q70=makeQuery(id+"F0.imprint","IMPRINT",FACE,{"disambiguationData":[TD([[makeQuery(id+"F0.imprint","IMPRINT",EDGE,{"disambiguationData":[TD([[subQ2,-1.0]])],"derivedFrom":subQ1}),-1.0]])]});}
            var Q71;
            {var subQ0=sQuery(id+"F0.wireOp",EDGE,"E95");var subQ1=sQuery(id+"F0.wireOp",EDGE,"E91.trimOffspring");var subQ2=makeQuery(id+"F0.imprint","INTERSECT",VERTEX,{"derivedFrom":[subQ1,subQ0]});Q71=makeQuery(id+"F0.imprint","IMPRINT",FACE,{"disambiguationData":[TD([[makeQuery(id+"F0.imprint","IMPRINT",EDGE,{"disambiguationData":[TD([[subQ2,-1.0]])],"derivedFrom":subQ1}),1.0]])]});}
            var Q72;
            {var subQ0=sQuery(id+"F0.wireOp",EDGE,"E97.0");var subQ1=sQuery(id+"F0.wireOp",EDGE,"E91.trimOffspring");var subQ2=makeQuery(id+"F0.imprint","INTERSECT",VERTEX,{"derivedFrom":[subQ1,subQ0]});Q72=makeQuery(id+"F0.imprint","IMPRINT",FACE,{"disambiguationData":[TD([[makeQuery(id+"F0.imprint","IMPRINT",EDGE,{"disambiguationData":[TD([[subQ2,-1.0]])],"derivedFrom":subQ1}),1.0]])]});}
            var Q73;
            {var subQ0=sQuery(id+"F0.wireOp",EDGE,"E95");var subQ1=sQuery(id+"F0.wireOp",EDGE,"E91.trimOffspring");var subQ2=makeQuery(id+"F0.imprint","INTERSECT",VERTEX,{"derivedFrom":[subQ1,subQ0]});Q73=makeQuery(id+"F0.imprint","IMPRINT",FACE,{"disambiguationData":[TD([[makeQuery(id+"F0.imprint","IMPRINT",EDGE,{"disambiguationData":[TD([[subQ2,-1.0]])],"derivedFrom":subQ1}),-1.0]])]});}
            var Q74;
            {var subQ0=sQuery(id+"F0.wireOp",EDGE,"E100.trimOffspring");var subQ1=sQuery(id+"F0.wireOp",EDGE,"E91.trimOffspring");var subQ2=makeQuery(id+"F0.imprint","INTERSECT",VERTEX,{"derivedFrom":[subQ1,subQ0]});Q74=makeQuery(id+"F0.imprint","IMPRINT",FACE,{"disambiguationData":[TD([[makeQuery(id+"F0.imprint","IMPRINT",EDGE,{"disambiguationData":[TD([[subQ2,-1.0]])],"derivedFrom":subQ1}),-1.0]])]});}
            var Q75;
            {var subQ0=sQuery(id+"F0.wireOp",EDGE,"E96");var subQ1=sQuery(id+"F0.wireOp",EDGE,"E91.trimOffspring");var subQ2=makeQuery(id+"F0.imprint","INTERSECT",VERTEX,{"derivedFrom":[subQ1,subQ0]});Q75=makeQuery(id+"F0.imprint","IMPRINT",FACE,{"disambiguationData":[TD([[makeQuery(id+"F0.imprint","IMPRINT",EDGE,{"disambiguationData":[TD([[subQ2,-1.0]])],"derivedFrom":subQ1}),-1.0]])]});}
            var Q76;
            {var subQ0=sQuery(id+"F0.wireOp",EDGE,"E96");var subQ1=sQuery(id+"F0.wireOp",EDGE,"E91.trimOffspring");var subQ2=makeQuery(id+"F0.imprint","INTERSECT",VERTEX,{"derivedFrom":[subQ1,subQ0]});Q76=makeQuery(id+"F0.imprint","IMPRINT",FACE,{"disambiguationData":[TD([[makeQuery(id+"F0.imprint","IMPRINT",EDGE,{"disambiguationData":[TD([[subQ2,-1.0]])],"derivedFrom":subQ1}),1.0]])]});}
            var Q77;
            {var subQ0=sQuery(id+"F0.wireOp",EDGE,"E100.trimOffspring");var subQ1=sQuery(id+"F0.wireOp",EDGE,"E91.trimOffspring");var subQ2=makeQuery(id+"F0.imprint","INTERSECT",VERTEX,{"derivedFrom":[subQ1,subQ0]});Q77=makeQuery(id+"F0.imprint","IMPRINT",FACE,{"disambiguationData":[TD([[makeQuery(id+"F0.imprint","IMPRINT",EDGE,{"disambiguationData":[TD([[subQ2,-1.0]])],"derivedFrom":subQ1}),1.0]])]});}
            var Q78;
            Q78=makeQuery(id+"F0.imprint","IMPRINT",FACE,{"disambiguationData":[TD([[makeQuery(id+"F0.imprint","IMPRINT",EDGE,{"derivedFrom":sQuery(id+"F0.wireOp",EDGE,"E33")}),1.0]])]});
            var Q79;
            Q79=makeQuery(id+"F0.imprint","IMPRINT",FACE,{"disambiguationData":[TD([[makeQuery(id+"F0.imprint","IMPRINT",EDGE,{"derivedFrom":sQuery(id+"F0.wireOp",EDGE,"E34")}),1.0]])]});
            var Q80;
            Q80=makeQuery(id+"F0.imprint","IMPRINT",FACE,{"disambiguationData":[TD([[makeQuery(id+"F0.imprint","IMPRINT",EDGE,{"derivedFrom":sQuery(id+"F0.wireOp",EDGE,"E60")}),1.0]])]});
            var Q81;
            {var subQ0=sQuery(id+"F0.wireOp",EDGE,"E104");Q81=makeQuery(id+"F0.imprint","IMPRINT",FACE,{"disambiguationData":[TD([[makeQuery(id+"F0.imprint","IMPRINT",EDGE,{"derivedFrom":subQ0}),-1.0]])]});}
            var Q82;
            {var subQ0=sQuery(id+"F0.wireOp",EDGE,"E104");Q82=makeQuery(id+"F0.imprint","IMPRINT",FACE,{"disambiguationData":[TD([[makeQuery(id+"F0.imprint","IMPRINT",EDGE,{"derivedFrom":subQ0}),1.0]])]});}
            var Q83;
            {var subQ0=sQuery(id+"F0.wireOp",EDGE,"E103");Q83=makeQuery(id+"F0.imprint","IMPRINT",FACE,{"disambiguationData":[TD([[makeQuery(id+"F0.imprint","IMPRINT",EDGE,{"derivedFrom":subQ0}),-1.0]])]});}
            var Q84;
            {var subQ0=sQuery(id+"F0.wireOp",EDGE,"E103");Q84=makeQuery(id+"F0.imprint","IMPRINT",FACE,{"disambiguationData":[TD([[makeQuery(id+"F0.imprint","IMPRINT",EDGE,{"derivedFrom":subQ0}),1.0]])]});}
            var Q85;
            {var subQ0=sQuery(id+"F0.wireOp",EDGE,"E102");Q85=makeQuery(id+"F0.imprint","IMPRINT",FACE,{"disambiguationData":[TD([[makeQuery(id+"F0.imprint","IMPRINT",EDGE,{"derivedFrom":subQ0}),-1.0]])]});}
            var Q86;
            {var subQ0=sQuery(id+"F0.wireOp",EDGE,"E102");Q86=makeQuery(id+"F0.imprint","IMPRINT",FACE,{"disambiguationData":[TD([[makeQuery(id+"F0.imprint","IMPRINT",EDGE,{"derivedFrom":subQ0}),1.0]])]});}
            var Q87;
            Q87=makeQuery(id+"F0.imprint","IMPRINT",FACE,{"disambiguationData":[TD([[makeQuery(id+"F0.imprint","IMPRINT",EDGE,{"derivedFrom":sQuery(id+"F0.wireOp",EDGE,"E61")}),1.0]])]});
            extrude(context, id + "F1", {"entities" : qUnion([Q0, Q1, Q2, Q3, Q4, Q5, Q6, Q7, Q8, Q9, Q10, Q11, Q12, Q13, Q14, Q15, Q16, Q17, Q18, Q19, Q20, Q21, Q22, Q23, Q24, Q25, Q26, Q27, Q28, Q29, Q30, Q31, Q32, Q33, Q34, Q35, Q36, Q37, Q38, Q39, Q40, Q41, Q42, Q43, Q44, Q45, Q46, Q47, Q48, Q49, Q50, Q51, Q52, Q53, Q54, Q55, Q56, Q57, Q58, Q59, Q60, Q61, Q62, Q63, Q64, Q65, Q66, Q67, Q68, Q69, Q70, Q71, Q72, Q73, Q74, Q75, Q76, Q77, Q78, Q79, Q80, Q81, Q82, Q83, Q84, Q85, Q86, Q87]), "depth" : 2.54 * mm});
        }
        {
            var Q0;
            Q0=makeQuery(id+"F1.opExtrude","CAP_EDGE",EDGE,{"disambiguationData":[OSD([sQuery(id+"F0.wireOp",EDGE,"E62")])],"isStart":false});
            var Q1;
            Q1=makeQuery(id+"F1.opExtrude","CAP_EDGE",EDGE,{"disambiguationData":[OSD([sQuery(id+"F0.wireOp",EDGE,"E63")])],"isStart":false});
            var Q2;
            Q2=makeQuery(id+"F1.opExtrude","CAP_EDGE",EDGE,{"disambiguationData":[OSD([sQuery(id+"F0.wireOp",EDGE,"E64")])],"isStart":false});
            var Q3;
            Q3=makeQuery(id+"F1.opExtrude","CAP_EDGE",EDGE,{"disambiguationData":[OSD([sQuery(id+"F0.wireOp",EDGE,"E40")])],"isStart":false});
            var Q4;
            Q4=makeQuery(id+"F1.opExtrude","CAP_EDGE",EDGE,{"disambiguationData":[OSD([sQuery(id+"F0.wireOp",EDGE,"E39")])],"isStart":false});
            var Q5;
            Q5=makeQuery(id+"F1.opExtrude","CAP_EDGE",EDGE,{"disambiguationData":[OSD([sQuery(id+"F0.wireOp",EDGE,"E38")])],"isStart":false});
            var Q6;
            Q6=makeQuery(id+"F1.opExtrude","CAP_EDGE",EDGE,{"disambiguationData":[OSD([sQuery(id+"F0.wireOp",EDGE,"E54")])],"isStart":false});
            fillet(context, id + "F2", {"entities" : qUnion([Q0, Q1, Q2, Q3, Q4, Q5, Q6]), "radius" : 0.71 * mm, "tangentPropagation" : true, "allowEdgeOverflow" : false});
        }
        {
            var Q0;
            Q0=makeQuery(id+"F1.opExtrude","CAP_EDGE",EDGE,{"disambiguationData":[OSD([sQuery(id+"F0.wireOp",EDGE,"E57")])],"isStart":false});
            var Q1;
            Q1=makeQuery(id+"F1.opExtrude","CAP_EDGE",EDGE,{"disambiguationData":[OSD([sQuery(id+"F0.wireOp",EDGE,"E58")])],"isStart":false});
            var Q2;
            Q2=makeQuery(id+"F1.opExtrude","CAP_EDGE",EDGE,{"disambiguationData":[OSD([sQuery(id+"F0.wireOp",EDGE,"E59")])],"isStart":false});
            fillet(context, id + "F3", {"entities" : qUnion([Q0, Q1, Q2]), "radius" : 0.5 * mm, "tangentPropagation" : true, "allowEdgeOverflow" : false});
        }
        {
            var Q0;
            Q0=makeQuery(id+"F1.opExtrude","CAP_EDGE",EDGE,{"disambiguationData":[OSD([sQuery(id+"F0.wireOp",EDGE,"E55")])],"isStart":false});
            var Q1;
            Q1=makeQuery(id+"F1.opExtrude","CAP_EDGE",EDGE,{"disambiguationData":[OSD([sQuery(id+"F0.wireOp",EDGE,"E33")])],"isStart":false});
            var Q2;
            Q2=makeQuery(id+"F1.opExtrude","CAP_EDGE",EDGE,{"disambiguationData":[OSD([sQuery(id+"F0.wireOp",EDGE,"E34")])],"isStart":false});
            var Q3;
            Q3=makeQuery(id+"F1.opExtrude","CAP_EDGE",EDGE,{"disambiguationData":[OSD([sQuery(id+"F0.wireOp",EDGE,"E60")])],"isStart":false});
            var Q4;
            Q4=makeQuery(id+"F1.opExtrude","CAP_EDGE",EDGE,{"disambiguationData":[OSD([sQuery(id+"F0.wireOp",EDGE,"E61")])],"isStart":false});
            fillet(context, id + "F4", {"entities" : qUnion([Q0, Q1, Q2, Q3, Q4]), "radius" : 0.57 * mm, "tangentPropagation" : true, "allowEdgeOverflow" : false});
        }
        {
            var Q0;
            Q0=makeQuery(id+"F1.opExtrude","CAP_EDGE",EDGE,{"disambiguationData":[OSD([sQuery(id+"F0.wireOp",EDGE,"E67")])],"isStart":false});
            var Q1;
            Q1=makeQuery(id+"F1.opExtrude","CAP_EDGE",EDGE,{"disambiguationData":[OSD([sQuery(id+"F0.wireOp",EDGE,"E65")])],"isStart":false});
            var Q2;
            Q2=makeQuery(id+"F1.opExtrude","CAP_EDGE",EDGE,{"disambiguationData":[OSD([sQuery(id+"F0.wireOp",EDGE,"E56")])],"isStart":false});
            fillet(context, id + "F5", {"entities" : qUnion([Q0, Q1, Q2]), "radius" : 0.46 * mm, "tangentPropagation" : true, "allowEdgeOverflow" : false});
        }
        {
            var Q0;
            Q0=makeQuery(id+"F1.opExtrude","CAP_EDGE",EDGE,{"disambiguationData":[OSD([sQuery(id+"F0.wireOp",EDGE,"E66")])],"isStart":false});
            fillet(context, id + "F6", {"entities" : qUnion([Q0]), "radius" : 0.76 * mm, "tangentPropagation" : true, "allowEdgeOverflow" : false});
        }
        {
            var Q0;
            Q0=makeQuery(id+"F1.opExtrude","CAP_EDGE",EDGE,{"disambiguationData":[OSD([sQuery(id+"F0.wireOp",EDGE,"E47.0")])],"isStart":false});
            var Q1;
            Q1=makeQuery(id+"F1.opExtrude","CAP_EDGE",EDGE,{"disambiguationData":[OSD([sQuery(id+"F0.wireOp",EDGE,"E9")])],"isStart":false});
            var Q2;
            Q2=makeQuery(id+"F1.opExtrude","CAP_EDGE",EDGE,{"disambiguationData":[OSD([sQuery(id+"F0.wireOp",EDGE,"E37.0")])],"isStart":false});
            var Q3;
            {var subQ0=sQuery(id+"F0.wireOp",EDGE,"E1");Q3=makeQuery(id+"F1.opExtrude","CAP_EDGE",EDGE,{"disambiguationData":[OSD([subQ0]),TDD([makeQuery(id+"F0.imprint","IMPRINT",EDGE,{"disambiguationData":[TD([[makeQuery(id+"F0.imprint","INTERSECT",VERTEX,{"derivedFrom":[subQ0,sQuery(id+"F0.wireOp",EDGE,"E105.0")]}),1.0]])],"derivedFrom":subQ0})])],"isStart":false});}
            var Q4;
            Q4=makeQuery(id+"F1.opExtrude","CAP_EDGE",EDGE,{"disambiguationData":[OSD([sQuery(id+"F0.wireOp",EDGE,"E32")])],"isStart":false});
            var Q5;
            {var subQ0=sQuery(id+"F0.wireOp",EDGE,"E36.0");Q5=makeQuery(id+"F1.opExtrude","CAP_EDGE",EDGE,{"disambiguationData":[OSD([subQ0]),TDD([makeQuery(id+"F0.imprint","IMPRINT",EDGE,{"disambiguationData":[TD([[makeQuery(id+"F0.imprint","INTERSECT",VERTEX,{"disambiguationData":[OD(1.0)],"derivedFrom":[subQ0,sQuery(id+"F0.wireOp",EDGE,"E36.1")]}),1.0]])],"derivedFrom":subQ0})])],"isStart":false});}
            var Q6;
            Q6=makeQuery(id+"F1.opExtrude","CAP_EDGE",EDGE,{"disambiguationData":[OSD([sQuery(id+"F0.wireOp",EDGE,"E110.0")])],"isStart":false});
            var Q7;
            Q7=makeQuery(id+"F1.opExtrude","CAP_FACE",FACE,{"disambiguationData":[OSD([sQuery(id+"F0.wireOp",EDGE,"E10"),sQuery(id+"F0.wireOp",EDGE,"E48.0")])],"isStart":false});
            var Q8;
            Q8=makeQuery(id+"F1.opExtrude","CAP_EDGE",EDGE,{"disambiguationData":[OSD([sQuery(id+"F0.wireOp",EDGE,"E21")])],"isStart":false});
            var Q9;
            Q9=makeQuery(id+"F1.opExtrude","CAP_EDGE",EDGE,{"disambiguationData":[OSD([sQuery(id+"F0.wireOp",EDGE,"E36.1")])],"isStart":false});
            var Q10;
            {var subQ0=sQuery(id+"F0.wireOp",EDGE,"E36.0");Q10=makeQuery(id+"F1.opExtrude","CAP_EDGE",EDGE,{"disambiguationData":[OSD([subQ0]),TDD([makeQuery(id+"F0.imprint","IMPRINT",EDGE,{"disambiguationData":[TD([[makeQuery(id+"F0.imprint","INTERSECT",VERTEX,{"disambiguationData":[OD(0.0)],"derivedFrom":[subQ0,sQuery(id+"F0.wireOp",EDGE,"E36.1")]}),-1.0]])],"derivedFrom":subQ0})])],"isStart":false});}
            var Q11;
            Q11=makeQuery(id+"F1.opExtrude","CAP_EDGE",EDGE,{"disambiguationData":[OSD([sQuery(id+"F0.wireOp",EDGE,"E105.0")])],"isStart":false});
            var Q12;
            {var subQ0=sQuery(id+"F0.wireOp",EDGE,"E36.0");Q12=makeQuery(id+"F1.opExtrude","CAP_EDGE",EDGE,{"disambiguationData":[OSD([subQ0]),TDD([makeQuery(id+"F0.imprint","IMPRINT",EDGE,{"disambiguationData":[TD([[makeQuery(id+"F0.imprint","INTERSECT",VERTEX,{"derivedFrom":[subQ0,sQuery(id+"F0.wireOp",EDGE,"E106.0")]}),-1.0]])],"derivedFrom":subQ0})])],"isStart":false});}
            var Q13;
            Q13=makeQuery(id+"F1.opExtrude","CAP_EDGE",EDGE,{"disambiguationData":[OSD([sQuery(id+"F0.wireOp",EDGE,"E108.0")])],"isStart":false});
            var Q14;
            Q14=makeQuery(id+"F1.opExtrude","CAP_EDGE",EDGE,{"disambiguationData":[OSD([sQuery(id+"F0.wireOp",EDGE,"E106.0")])],"isStart":false});
            var Q15;
            {var subQ0=sQuery(id+"F0.wireOp",EDGE,"E1");Q15=makeQuery(id+"F1.opExtrude","CAP_EDGE",EDGE,{"disambiguationData":[OSD([subQ0]),TDD([makeQuery(id+"F0.imprint","IMPRINT",EDGE,{"disambiguationData":[TD([[makeQuery(id+"F0.imprint","INTERSECT",VERTEX,{"derivedFrom":[subQ0,sQuery(id+"F0.wireOp",EDGE,"E106.0")]}),-1.0]])],"derivedFrom":subQ0})])],"isStart":false});}
            var Q16;
            Q16=makeQuery(id+"F1.opExtrude","CAP_EDGE",EDGE,{"disambiguationData":[OSD([sQuery(id+"F0.wireOp",EDGE,"E107.0")])],"isStart":false});
            var Q17;
            {var subQ0=sQuery(id+"F0.wireOp",EDGE,"E36.0");Q17=makeQuery(id+"F1.opExtrude","CAP_EDGE",EDGE,{"disambiguationData":[OSD([subQ0]),TDD([makeQuery(id+"F0.imprint","IMPRINT",EDGE,{"disambiguationData":[TD([[makeQuery(id+"F0.imprint","INTERSECT",VERTEX,{"derivedFrom":[subQ0,sQuery(id+"F0.wireOp",EDGE,"E107.0")]}),-1.0]])],"derivedFrom":subQ0})])],"isStart":false});}
            var Q18;
            {var subQ0=sQuery(id+"F0.wireOp",EDGE,"E1");Q18=makeQuery(id+"F1.opExtrude","CAP_EDGE",EDGE,{"disambiguationData":[OSD([subQ0]),TDD([makeQuery(id+"F0.imprint","IMPRINT",EDGE,{"disambiguationData":[TD([[makeQuery(id+"F0.imprint","INTERSECT",VERTEX,{"derivedFrom":[subQ0,sQuery(id+"F0.wireOp",EDGE,"E107.0")]}),-1.0]])],"derivedFrom":subQ0})])],"isStart":false});}
            var Q19;
            Q19=makeQuery(id+"F1.opExtrude","CAP_EDGE",EDGE,{"disambiguationData":[OSD([sQuery(id+"F0.wireOp",EDGE,"E109.0")])],"isStart":false});
            var Q20;
            Q20=makeQuery(id+"F1.opExtrude","CAP_FACE",FACE,{"disambiguationData":[OSD([sQuery(id+"F0.wireOp",EDGE,"E2"),sQuery(id+"F0.wireOp",EDGE,"E35.0")])],"isStart":false});
            var Q21;
            Q21=makeQuery(id+"F1.opExtrude","CAP_FACE",FACE,{"disambiguationData":[OSD([sQuery(id+"F0.wireOp",EDGE,"E5"),sQuery(id+"F0.wireOp",EDGE,"E18"),sQuery(id+"F0.wireOp",EDGE,"E19"),sQuery(id+"F0.wireOp",EDGE,"E20.trimOffspring"),sQuery(id+"F0.wireOp",EDGE,"E23"),sQuery(id+"F0.wireOp",EDGE,"E24.trimOffspring"),sQuery(id+"F0.wireOp",EDGE,"E25"),sQuery(id+"F0.wireOp",EDGE,"E26.trimOffspring"),sQuery(id+"F0.wireOp",EDGE,"E41.0"),sQuery(id+"F0.wireOp",EDGE,"E41.1"),sQuery(id+"F0.wireOp",EDGE,"E41.2"),sQuery(id+"F0.wireOp",EDGE,"E41.3"),sQuery(id+"F0.wireOp",EDGE,"E41.4"),sQuery(id+"F0.wireOp",EDGE,"E41.5"),sQuery(id+"F0.wireOp",EDGE,"E41.6"),sQuery(id+"F0.wireOp",EDGE,"E41.7"),sQuery(id+"F0.wireOp",EDGE,"E45"),sQuery(id+"F0.wireOp",EDGE,"E46.0"),sQuery(id+"F0.wireOp",EDGE,"E87.0"),sQuery(id+"F0.wireOp",EDGE,"E88.0"),sQuery(id+"F0.wireOp",EDGE,"E89.0"),sQuery(id+"F0.wireOp",EDGE,"E90.0"),sQuery(id+"F0.wireOp",EDGE,"E92.0"),sQuery(id+"F0.wireOp",EDGE,"E93.0"),sQuery(id+"F0.wireOp",EDGE,"E97.0"),sQuery(id+"F0.wireOp",EDGE,"E98.0"),sQuery(id+"F0.wireOp",EDGE,"E99.0"),sQuery(id+"F0.wireOp",EDGE,"E100.trimOffspring")])],"isStart":false});
            var Q22;
            Q22=makeQuery(id+"F1.opExtrude","CAP_FACE",FACE,{"disambiguationData":[OSD([sQuery(id+"F0.wireOp",EDGE,"E12"),sQuery(id+"F0.wireOp",EDGE,"E50.0")])],"isStart":false});
            var Q23;
            Q23=makeQuery(id+"F1.opExtrude","CAP_FACE",FACE,{"disambiguationData":[OSD([sQuery(id+"F0.wireOp",EDGE,"E16"),sQuery(id+"F0.wireOp",EDGE,"E49.0")])],"isStart":false});
            var Q24;
            Q24=makeQuery(id+"F1.opExtrude","CAP_FACE",FACE,{"disambiguationData":[OSD([sQuery(id+"F0.wireOp",EDGE,"E17"),sQuery(id+"F0.wireOp",EDGE,"E53.0")])],"isStart":false});
            var Q25;
            Q25=makeQuery(id+"F1.opExtrude","CAP_FACE",FACE,{"disambiguationData":[OSD([sQuery(id+"F0.wireOp",EDGE,"E4"),sQuery(id+"F0.wireOp",EDGE,"E11"),sQuery(id+"F0.wireOp",EDGE,"E13"),sQuery(id+"F0.wireOp",EDGE,"E14"),sQuery(id+"F0.wireOp",EDGE,"E15"),sQuery(id+"F0.wireOp",EDGE,"E27"),sQuery(id+"F0.wireOp",EDGE,"E28"),sQuery(id+"F0.wireOp",EDGE,"E29.trimOffspring"),sQuery(id+"F0.wireOp",EDGE,"E30"),sQuery(id+"F0.wireOp",EDGE,"E31.trimOffspring"),sQuery(id+"F0.wireOp",EDGE,"E42.0"),sQuery(id+"F0.wireOp",EDGE,"E42.1"),sQuery(id+"F0.wireOp",EDGE,"E42.2"),sQuery(id+"F0.wireOp",EDGE,"E42.3"),sQuery(id+"F0.wireOp",EDGE,"E42.4"),sQuery(id+"F0.wireOp",EDGE,"E42.5"),sQuery(id+"F0.wireOp",EDGE,"E43.0"),sQuery(id+"F0.wireOp",EDGE,"E44.0"),sQuery(id+"F0.wireOp",EDGE,"E51.0"),sQuery(id+"F0.wireOp",EDGE,"E52.0"),sQuery(id+"F0.wireOp",EDGE,"E69.0"),sQuery(id+"F0.wireOp",EDGE,"E70.0"),sQuery(id+"F0.wireOp",EDGE,"E72.0"),sQuery(id+"F0.wireOp",EDGE,"E73.0"),sQuery(id+"F0.wireOp",EDGE,"E75.0"),sQuery(id+"F0.wireOp",EDGE,"E76.0"),sQuery(id+"F0.wireOp",EDGE,"E80.0"),sQuery(id+"F0.wireOp",EDGE,"E81.0"),sQuery(id+"F0.wireOp",EDGE,"E82.0"),sQuery(id+"F0.wireOp",EDGE,"E83.0")])],"isStart":false});
            fillet(context, id + "F7", {"entities" : qUnion([Q0, Q1, Q2, Q3, Q4, Q5, Q6, Q7, Q8, Q9, Q10, Q11, Q12, Q13, Q14, Q15, Q16, Q17, Q18, Q19, Q20, Q21, Q22, Q23, Q24, Q25]), "radius" : 0.37 * mm, "tangentPropagation" : true, "allowEdgeOverflow" : false});
        }
        {
            var Q0;
            Q0=makeQuery(id+"F1.opExtrude","CAP_FACE",FACE,{"disambiguationData":[OSD([sQuery(id+"F0.wireOp",EDGE,"E0"),sQuery(id+"F0.wireOp",EDGE,"E3"),sQuery(id+"F0.wireOp",EDGE,"E111"),sQuery(id+"F0.wireOp",EDGE,"E112"),sQuery(id+"F0.wireOp",EDGE,"E113"),sQuery(id+"F0.wireOp",EDGE,"E114.trimOffspring"),sQuery(id+"F0.wireOp",EDGE,"E115.trimOffspring")])],"isStart":false});
            fillet(context, id + "F8", {"entities" : qUnion([Q0]), "radius" : 0.5 * mm, "tangentPropagation" : true, "allowEdgeOverflow" : false});
        }
        {
            var Q0;
            Q0=makeQuery(id+"F0.imprint","IMPRINT",FACE,{"disambiguationData":[TD([[makeQuery(id+"F0.imprint","IMPRINT",EDGE,{"derivedFrom":sQuery(id+"F0.wireOp",EDGE,"E3")}),1.0]])]});
            var Q1;
            {var subQ4=sQuery(id+"F0.wireOp",EDGE,"E42.0");Q1=makeQuery(id+"F0.imprint","IMPRINT",FACE,{"disambiguationData":[TD([[makeQuery(id+"F0.imprint","IMPRINT",EDGE,{"derivedFrom":subQ4}),1.0]])]});}
            var Q2;
            Q2=makeQuery(id+"F0.imprint","IMPRINT",FACE,{"disambiguationData":[TD([[makeQuery(id+"F0.imprint","IMPRINT",EDGE,{"derivedFrom":sQuery(id+"F0.wireOp",EDGE,"E51.0")}),1.0]])]});
            var Q3;
            Q3=makeQuery(id+"F0.imprint","IMPRINT",FACE,{"disambiguationData":[TD([[makeQuery(id+"F0.imprint","IMPRINT",EDGE,{"derivedFrom":sQuery(id+"F0.wireOp",EDGE,"E12")}),-1.0]])]});
            var Q4;
            Q4=makeQuery(id+"F0.imprint","IMPRINT",FACE,{"disambiguationData":[TD([[makeQuery(id+"F0.imprint","IMPRINT",EDGE,{"derivedFrom":sQuery(id+"F0.wireOp",EDGE,"E17")}),1.0]])]});
            var Q5;
            Q5=makeQuery(id+"F0.imprint","IMPRINT",FACE,{"disambiguationData":[TD([[makeQuery(id+"F0.imprint","IMPRINT",EDGE,{"derivedFrom":sQuery(id+"F0.wireOp",EDGE,"E65")}),-1.0]])]});
            var Q6;
            {var subQ0=sQuery(id+"F0.wireOp",EDGE,"E70.0");var subQ1=sQuery(id+"F0.wireOp",EDGE,"E14");var subQ2=makeQuery(id+"F0.imprint","INTERSECT",VERTEX,{"derivedFrom":[subQ1,subQ0]});Q6=makeQuery(id+"F0.imprint","IMPRINT",FACE,{"disambiguationData":[TD([[makeQuery(id+"F0.imprint","IMPRINT",EDGE,{"disambiguationData":[TD([[subQ2,1.0]])],"derivedFrom":subQ1}),-1.0]])]});}
            var Q7;
            {var subQ3=sQuery(id+"F0.wireOp",EDGE,"E76.0");Q7=makeQuery(id+"F0.imprint","IMPRINT",FACE,{"disambiguationData":[TD([[makeQuery(id+"F0.imprint","IMPRINT",EDGE,{"derivedFrom":subQ3}),1.0]])]});}
            var Q8;
            Q8=makeQuery(id+"F0.imprint","IMPRINT",FACE,{"disambiguationData":[TD([[makeQuery(id+"F0.imprint","IMPRINT",EDGE,{"derivedFrom":sQuery(id+"F0.wireOp",EDGE,"E50.0")}),1.0]])]});
            var Q9;
            Q9=makeQuery(id+"F0.imprint","IMPRINT",FACE,{"disambiguationData":[TD([[makeQuery(id+"F0.imprint","IMPRINT",EDGE,{"derivedFrom":sQuery(id+"F0.wireOp",EDGE,"E16")}),1.0]])]});
            var Q10;
            Q10=makeQuery(id+"F0.imprint","IMPRINT",FACE,{"disambiguationData":[TD([[makeQuery(id+"F0.imprint","IMPRINT",EDGE,{"derivedFrom":sQuery(id+"F0.wireOp",EDGE,"E13")}),1.0]])]});
            var Q11;
            {var subQ0=sQuery(id+"F0.wireOp",EDGE,"E81.0");Q11=makeQuery(id+"F0.imprint","IMPRINT",FACE,{"disambiguationData":[TD([[makeQuery(id+"F0.imprint","IMPRINT",EDGE,{"derivedFrom":subQ0}),1.0]])]});}
            var Q12;
            Q12=makeQuery(id+"F0.imprint","IMPRINT",FACE,{"disambiguationData":[TD([[makeQuery(id+"F0.imprint","IMPRINT",EDGE,{"derivedFrom":sQuery(id+"F0.wireOp",EDGE,"E9")}),1.0]])]});
            var Q13;
            Q13=makeQuery(id+"F0.imprint","IMPRINT",FACE,{"disambiguationData":[TD([[makeQuery(id+"F0.imprint","IMPRINT",EDGE,{"derivedFrom":sQuery(id+"F0.wireOp",EDGE,"E10")}),1.0]])]});
            var Q14;
            {var subQ7=sQuery(id+"F0.wireOp",EDGE,"E41.7");Q14=makeQuery(id+"F0.imprint","IMPRINT",FACE,{"disambiguationData":[TD([[makeQuery(id+"F0.imprint","IMPRINT",EDGE,{"derivedFrom":subQ7}),-1.0]])]});}
            var Q15;
            {var subQ0=sQuery(id+"F0.wireOp",EDGE,"E97.0");var subQ1=sQuery(id+"F0.wireOp",EDGE,"E41.3");var subQ2=makeQuery(id+"F0.imprint","INTERSECT",VERTEX,{"derivedFrom":[subQ1,subQ0]});Q15=makeQuery(id+"F0.imprint","IMPRINT",FACE,{"disambiguationData":[TD([[makeQuery(id+"F0.imprint","IMPRINT",EDGE,{"disambiguationData":[TD([[subQ2,1.0]])],"derivedFrom":subQ1}),1.0]])]});}
            var Q16;
            {var subQ5=sQuery(id+"F0.wireOp",EDGE,"E41.1");Q16=makeQuery(id+"F0.imprint","IMPRINT",FACE,{"disambiguationData":[TD([[makeQuery(id+"F0.imprint","IMPRINT",EDGE,{"derivedFrom":subQ5}),-1.0]])]});}
            var Q17;
            {var subQ0=sQuery(id+"F0.wireOp",EDGE,"E88.0");Q17=makeQuery(id+"F0.imprint","IMPRINT",FACE,{"disambiguationData":[TD([[makeQuery(id+"F0.imprint","IMPRINT",EDGE,{"derivedFrom":subQ0}),1.0]])]});}
            var Q18;
            {var subQ3=sQuery(id+"F0.wireOp",EDGE,"E89.0");Q18=makeQuery(id+"F0.imprint","IMPRINT",FACE,{"disambiguationData":[TD([[makeQuery(id+"F0.imprint","IMPRINT",EDGE,{"derivedFrom":subQ3}),-1.0]])]});}
            var Q19;
            {var subQ0=sQuery(id+"F0.wireOp",EDGE,"E41.4");Q19=makeQuery(id+"F0.imprint","IMPRINT",FACE,{"disambiguationData":[TD([[makeQuery(id+"F0.imprint","IMPRINT",EDGE,{"derivedFrom":subQ0}),1.0]])]});}
            var Q20;
            {var subQ5=sQuery(id+"F0.wireOp",EDGE,"E41.6");var subQ6=sQuery(id+"F0.wireOp",EDGE,"E41.5");var subQ7=makeQuery(id+"F0.imprint","INTERSECT",VERTEX,{"derivedFrom":[subQ6,subQ5]});Q20=makeQuery(id+"F0.imprint","IMPRINT",FACE,{"disambiguationData":[TD([[makeQuery(id+"F0.imprint","IMPRINT",EDGE,{"disambiguationData":[TD([[subQ7,1.0]])],"derivedFrom":subQ6}),-1.0]])]});}
            var Q21;
            {var subQ0=sQuery(id+"F0.wireOp",EDGE,"E45");var subQ1=sQuery(id+"F0.wireOp",EDGE,"E41.6");var subQ2=makeQuery(id+"F0.imprint","INTERSECT",VERTEX,{"disambiguationData":[OD(0.0)],"derivedFrom":[subQ1,subQ0]});Q21=makeQuery(id+"F0.imprint","IMPRINT",FACE,{"disambiguationData":[TD([[makeQuery(id+"F0.imprint","IMPRINT",EDGE,{"disambiguationData":[TD([[subQ2,-1.0]])],"derivedFrom":subQ1}),1.0]])]});}
            var Q22;
            {var subQ0=sQuery(id+"F0.wireOp",EDGE,"E45");var subQ1=sQuery(id+"F0.wireOp",EDGE,"E26.trimOffspring");var subQ2=makeQuery(id+"F0.imprint","INTERSECT",VERTEX,{"disambiguationData":[OD(0.0)],"derivedFrom":[subQ1,subQ0]});Q22=makeQuery(id+"F0.imprint","IMPRINT",FACE,{"disambiguationData":[TD([[makeQuery(id+"F0.imprint","IMPRINT",EDGE,{"disambiguationData":[TD([[subQ2,-1.0]])],"derivedFrom":subQ1}),-1.0]])]});}
            var Q23;
            {var subQ0=sQuery(id+"F0.wireOp",EDGE,"E97.0");var subQ1=sQuery(id+"F0.wireOp",EDGE,"E92.0");var subQ2=makeQuery(id+"F0.imprint","INTERSECT",VERTEX,{"derivedFrom":[subQ1,subQ0]});Q23=makeQuery(id+"F0.imprint","IMPRINT",FACE,{"disambiguationData":[TD([[makeQuery(id+"F0.imprint","IMPRINT",EDGE,{"disambiguationData":[TD([[subQ2,-1.0]])],"derivedFrom":subQ1}),-1.0]])]});}
            var Q24;
            Q24=makeQuery(id+"F0.imprint","IMPRINT",FACE,{"disambiguationData":[TD([[makeQuery(id+"F0.imprint","IMPRINT",EDGE,{"derivedFrom":sQuery(id+"F0.wireOp",EDGE,"E2")}),-1.0]])]});
            var Q25;
            Q25=makeQuery(id+"F0.imprint","IMPRINT",FACE,{"disambiguationData":[TD([[makeQuery(id+"F0.imprint","IMPRINT",EDGE,{"derivedFrom":sQuery(id+"F0.wireOp",EDGE,"E33")}),-1.0]])]});
            var Q26;
            Q26=makeQuery(id+"F0.imprint","IMPRINT",FACE,{"disambiguationData":[TD([[makeQuery(id+"F0.imprint","IMPRINT",EDGE,{"derivedFrom":sQuery(id+"F0.wireOp",EDGE,"E37.0")}),1.0]])]});
            var Q27;
            {var subQ0=sQuery(id+"F0.wireOp",EDGE,"E107.0");Q27=makeQuery(id+"F0.imprint","IMPRINT",FACE,{"disambiguationData":[TD([[makeQuery(id+"F0.imprint","IMPRINT",EDGE,{"derivedFrom":subQ0}),1.0]])]});}
            var Q28;
            {var subQ0=sQuery(id+"F0.wireOp",EDGE,"E106.0");Q28=makeQuery(id+"F0.imprint","IMPRINT",FACE,{"disambiguationData":[TD([[makeQuery(id+"F0.imprint","IMPRINT",EDGE,{"derivedFrom":subQ0}),1.0]])]});}
            extrude(context, id + "F9", {"entities" : qUnion([Q0, Q1, Q2, Q3, Q4, Q5, Q6, Q7, Q8, Q9, Q10, Q11, Q12, Q13, Q14, Q15, Q16, Q17, Q18, Q19, Q20, Q21, Q22, Q23, Q24, Q25, Q26, Q27, Q28]), "depth" : 1.78 * mm});
        }
    });
